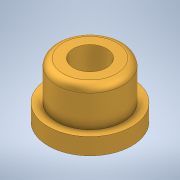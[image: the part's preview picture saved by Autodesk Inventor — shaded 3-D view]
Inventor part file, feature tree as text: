
AUTODESK INVENTOR PART (.ipt)
format: ipt  version: 2022 (Build 260153000, 153)  size: 135,168 bytes
history: native  units: mm
features: extrude x2, sketch x2, fillet x1
ambient origin geometry x8: Origin, YZ Plane, XZ Plane, XY Plane, X Axis, Y Axis, Z Axis, Center Point
bodies: Solid1 (feature_tree)
feature tree (5):
  extrude  "Extrusion1"  Depth=10.0mm
  extrude  "Extrusion2"  Depth=2.0mm
  fillet  "Fillet1"  Radius=5.0mm
  sketch  "Sketch1"  dims[d0=10.0mm d1=20.0mm]
  sketch  "Sketch2"  dims[d2=16.5mm d3=0.0mm d4=25.0mm d5=5.0mm d6=0.0mm d7=2.0mm d8=0.872665mm]
